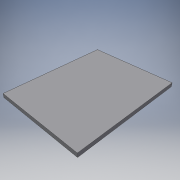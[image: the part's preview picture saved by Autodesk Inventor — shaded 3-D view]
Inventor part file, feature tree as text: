
AUTODESK INVENTOR PART (.ipt)
format: ipt  version: 2016 (Build 200138000, 138)  size: 87,552 bytes
history: native  units: in
note: dims shown in document units (in); Inventor stores cm internally (conversion verified against a paired STEP export)
features: extrude x1, sketch x1
ambient origin geometry x8: Origin, YZ Plane, XZ Plane, XY Plane, X Axis, Y Axis, Z Axis, Center Point
bodies: Solid1 (feature_tree)
feature tree (2):
  extrude  "Extrusion1"  Depth=20.0in
  sketch  "Sketch1"  dims[d0=16.0in d1=20.0in d2=0.75in d3=0.0in]
